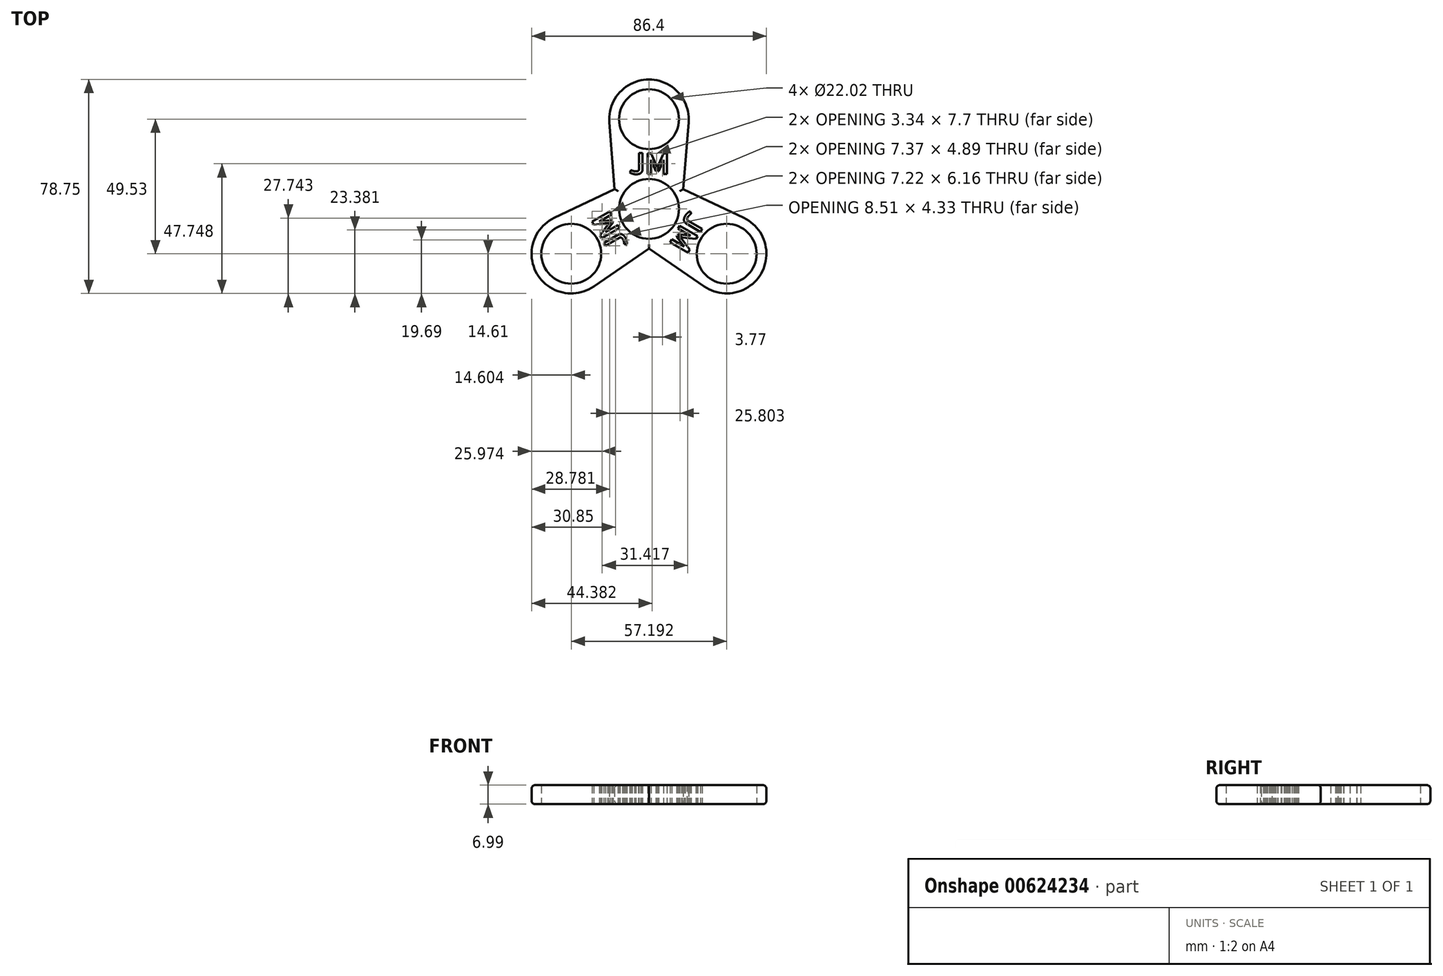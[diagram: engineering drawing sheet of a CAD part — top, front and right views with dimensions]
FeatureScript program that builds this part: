
annotation { "Feature Type Name" : "Feature", "Feature Type Description" : "" }
export const myFeature = defineFeature(function(context is Context, id is Id, definition is map)
    precondition{}
    {
        {
            var Q0;
            Q0=qCreatedBy(makeId("Top.planeOp"),FACE);
            var sketch = newSketch(context, id + "F0", { "sketchPlane" : qUnion([Q0])});
            skCircle(sketch, "E0", {"center": v(0, 0) * mm, "radius": 11.01 * mm});
            skCircle(sketch, "E1", {"center": v(0, 0) * mm, "radius": 14.6 * mm});
            skCircle(sketch, "E2.1.1", {"center": v(0, 33.02) * mm, "radius": 11.01 * mm});
            skCircle(sketch, "E3", {"center": v(0, 33.02) * mm, "radius": 14.6 * mm});
            skLineSegment(sketch, "E4", {"start": v(0, 33.02) * mm, "end": v(0, 0) * mm});
            skLineSegment(sketch, "E5", {"start": v(0, 0) * mm, "end": v(-28.6, -16.5) * mm});
            skLineSegment(sketch, "E6", {"start": v(0, 0) * mm, "end": v(28.6, -16.5) * mm});
            skCircle(sketch, "E7", {"center": v(-28.6, -16.5) * mm, "radius": 14.6 * mm});
            skCircle(sketch, "E8", {"center": v(-28.6, -16.5) * mm, "radius": 11.01 * mm});
            skCircle(sketch, "E9", {"center": v(28.6, -16.51) * mm, "radius": 14.6 * mm});
            skCircle(sketch, "E10", {"center": v(28.6, -16.51) * mm, "radius": 11.01 * mm});
            skLineSegment(sketch, "E11", {"start": v(-14.56, 31.89) * mm, "end": v(-12.65, 7.3) * mm});
            skLineSegment(sketch, "E12", {"start": v(-34.9, -3.33) * mm, "end": v(-12.65, 7.3) * mm});
            skLineSegment(sketch, "E13", {"start": v(14.56, 31.89) * mm, "end": v(12.65, 7.3) * mm});
            skLineSegment(sketch, "E14", {"start": v(12.65, 7.3) * mm, "end": v(34.9, -3.33) * mm});
            skLineSegment(sketch, "E15", {"start": v(-20.33, -28.55) * mm, "end": v(0, -14.6) * mm});
            skLineSegment(sketch, "E16", {"start": v(0, -14.6) * mm, "end": v(20.33, -28.55) * mm});
            skSolve(sketch);
        }
        {
            var Q0;
            Q0=makeQuery(id+"F0.imprint","IMPRINT",FACE,{"disambiguationData":[TD([[makeQuery(id+"F0.imprint","IMPRINT",EDGE,{"derivedFrom":sQuery(id+"F0.wireOp",EDGE,"E2.1.1")}),-1.0]])]});
            var Q1;
            {var subQ0=sQuery(id+"F0.wireOp",EDGE,"E11");Q1=makeQuery(id+"F0.imprint","IMPRINT",FACE,{"disambiguationData":[TD([[makeQuery(id+"F0.imprint","IMPRINT",EDGE,{"derivedFrom":subQ0}),1.0]])]});}
            var Q2;
            {var subQ0=sQuery(id+"F0.wireOp",EDGE,"E13");Q2=makeQuery(id+"F0.imprint","IMPRINT",FACE,{"disambiguationData":[TD([[makeQuery(id+"F0.imprint","IMPRINT",EDGE,{"derivedFrom":subQ0}),-1.0]])]});}
            var Q3;
            {var subQ1=sQuery(id+"F0.wireOp",EDGE,"E0");var subQ6=sQuery(id+"F0.wireOp",EDGE,"E5");var subQ8=makeQuery(id+"F0.imprint","INTERSECT",VERTEX,{"derivedFrom":[subQ1,subQ6]});Q3=makeQuery(id+"F0.imprint","IMPRINT",FACE,{"disambiguationData":[TD([[makeQuery(id+"F0.imprint","IMPRINT",EDGE,{"disambiguationData":[TD([[subQ8,1.0]])],"derivedFrom":subQ1}),-1.0]])]});}
            var Q4;
            {var subQ0=sQuery(id+"F0.wireOp",EDGE,"E5");var subQ1=sQuery(id+"F0.wireOp",EDGE,"E0");var subQ2=makeQuery(id+"F0.imprint","INTERSECT",VERTEX,{"derivedFrom":[subQ1,subQ0]});Q4=makeQuery(id+"F0.imprint","IMPRINT",FACE,{"disambiguationData":[TD([[makeQuery(id+"F0.imprint","IMPRINT",EDGE,{"disambiguationData":[TD([[subQ2,-1.0]])],"derivedFrom":subQ1}),-1.0]])]});}
            var Q5;
            {var subQ0=sQuery(id+"F0.wireOp",EDGE,"E14");Q5=makeQuery(id+"F0.imprint","IMPRINT",FACE,{"disambiguationData":[TD([[makeQuery(id+"F0.imprint","IMPRINT",EDGE,{"derivedFrom":subQ0}),-1.0]])]});}
            var Q6;
            {var subQ0=sQuery(id+"F0.wireOp",EDGE,"E4");var subQ1=sQuery(id+"F0.wireOp",EDGE,"E0");var subQ2=makeQuery(id+"F0.imprint","INTERSECT",VERTEX,{"derivedFrom":[subQ1,subQ0]});Q6=makeQuery(id+"F0.imprint","IMPRINT",FACE,{"disambiguationData":[TD([[makeQuery(id+"F0.imprint","IMPRINT",EDGE,{"disambiguationData":[TD([[subQ2,1.0]])],"derivedFrom":subQ1}),-1.0]])]});}
            var Q7;
            {var subQ0=sQuery(id+"F0.wireOp",EDGE,"E12");Q7=makeQuery(id+"F0.imprint","IMPRINT",FACE,{"disambiguationData":[TD([[makeQuery(id+"F0.imprint","IMPRINT",EDGE,{"derivedFrom":subQ0}),-1.0]])]});}
            var Q8;
            Q8=makeQuery(id+"F0.imprint","IMPRINT",FACE,{"disambiguationData":[TD([[makeQuery(id+"F0.imprint","IMPRINT",EDGE,{"derivedFrom":sQuery(id+"F0.wireOp",EDGE,"E8")}),-1.0]])]});
            var Q9;
            {var subQ0=sQuery(id+"F0.wireOp",EDGE,"E15");Q9=makeQuery(id+"F0.imprint","IMPRINT",FACE,{"disambiguationData":[TD([[makeQuery(id+"F0.imprint","IMPRINT",EDGE,{"derivedFrom":subQ0}),1.0]])]});}
            var Q10;
            {var subQ0=sQuery(id+"F0.wireOp",EDGE,"E16");Q10=makeQuery(id+"F0.imprint","IMPRINT",FACE,{"disambiguationData":[TD([[makeQuery(id+"F0.imprint","IMPRINT",EDGE,{"derivedFrom":subQ0}),1.0]])]});}
            var Q11;
            Q11=makeQuery(id+"F0.imprint","IMPRINT",FACE,{"disambiguationData":[TD([[makeQuery(id+"F0.imprint","IMPRINT",EDGE,{"derivedFrom":sQuery(id+"F0.wireOp",EDGE,"E10")}),-1.0]])]});
            extrude(context, id + "F1", {"entities" : qUnion([Q0, Q1, Q2, Q3, Q4, Q5, Q6, Q7, Q8, Q9, Q10, Q11]), "depth" : 7 * mm, "offsetDistance" : 25.4 * mm});
        }
        {
            var Q0;
            Q0=qCreatedBy(makeId("Top.planeOp"),FACE);
            var sketch = newSketch(context, id + "F2", { "sketchPlane" : qUnion([Q0])});
            skText(sketch, "E17", { "text": "JM", "fontName": "AllertaStencil-Regular.ttf"});
            skText(sketch, "E18", { "text": "JM", "fontName": "AllertaStencil-Regular.ttf"});
            skText(sketch, "E19", { "text": "JM", "fontName": "AllertaStencil-Regular.ttf"});
            skLineSegment(sketch, "E20", {"start": v(-0.13, -0.28) * mm, "end": v(-0.13, 8.64) * mm});
            skLineSegment(sketch, "E21", {"start": v(-0.13, 8.64) * mm, "end": v(-0.13, -0.28) * mm});
            skLineSegment(sketch, "E22", {"start": v(-0.13, -0.28) * mm, "end": v(8, -4.97) * mm});
            skLineSegment(sketch, "E23", {"start": v(-0.13, -0.28) * mm, "end": v(-7.13, -4.32) * mm});
            const initialGuessF2  = {"E17": [-0.00735, 0.01278, 1, 0, 0.0077], "E18": [0.01468, -0.00032, -0.5, -0.86603, 0.00761], "E19": [-0.00742, -0.01289, -0.5, 0.86603, 0.00761]};
            skSetInitialGuess(sketch, initialGuessF2);
            skSolve(sketch);
        }
        {
            var Q0;
            Q0 = qSketchRegion(id + "F2", true);
            extrude(context, id + "F3", {"entities" : qUnion([Q0]), "operationType" : NewBodyOperationType.REMOVE, "depth" : 7.06 * mm, "offsetDistance" : 25.4 * mm});
        }
        {
            var Q0;
            Q0=makeQuery(id+"F1.opExtrude","CAP_EDGE",EDGE,{"disambiguationData":[OSD([sQuery(id+"F0.wireOp",EDGE,"E12")])],"isStart":false});
            var Q1;
            Q1=makeQuery(id+"F1.opExtrude","CAP_EDGE",EDGE,{"disambiguationData":[OSD([sQuery(id+"F0.wireOp",EDGE,"E11")])],"isStart":false});
            var Q2;
            Q2=makeQuery(id+"F1.opExtrude","CAP_EDGE",EDGE,{"disambiguationData":[OSD([sQuery(id+"F0.wireOp",EDGE,"E14")])],"isStart":false});
            fillet(context, id + "F4", {"entities" : qUnion([Q0, Q1, Q2]), "radius" : 1.27 * mm, "tangentPropagation" : true, "allowEdgeOverflow" : false});
        }
        {
            var Q0;
            Q0=makeQuery(id+"F1.opExtrude","CAP_EDGE",EDGE,{"disambiguationData":[OSD([sQuery(id+"F0.wireOp",EDGE,"E13")])],"isStart":true});
            var Q1;
            Q1=makeQuery(id+"F1.opExtrude","CAP_EDGE",EDGE,{"disambiguationData":[OSD([sQuery(id+"F0.wireOp",EDGE,"E12")])],"isStart":true});
            var Q2;
            Q2=makeQuery(id+"F1.opExtrude","CAP_EDGE",EDGE,{"disambiguationData":[OSD([sQuery(id+"F0.wireOp",EDGE,"E16")])],"isStart":true});
            fillet(context, id + "F5", {"entities" : qUnion([Q0, Q1, Q2]), "radius" : 1.27 * mm, "tangentPropagation" : true, "allowEdgeOverflow" : false});
        }
    });
